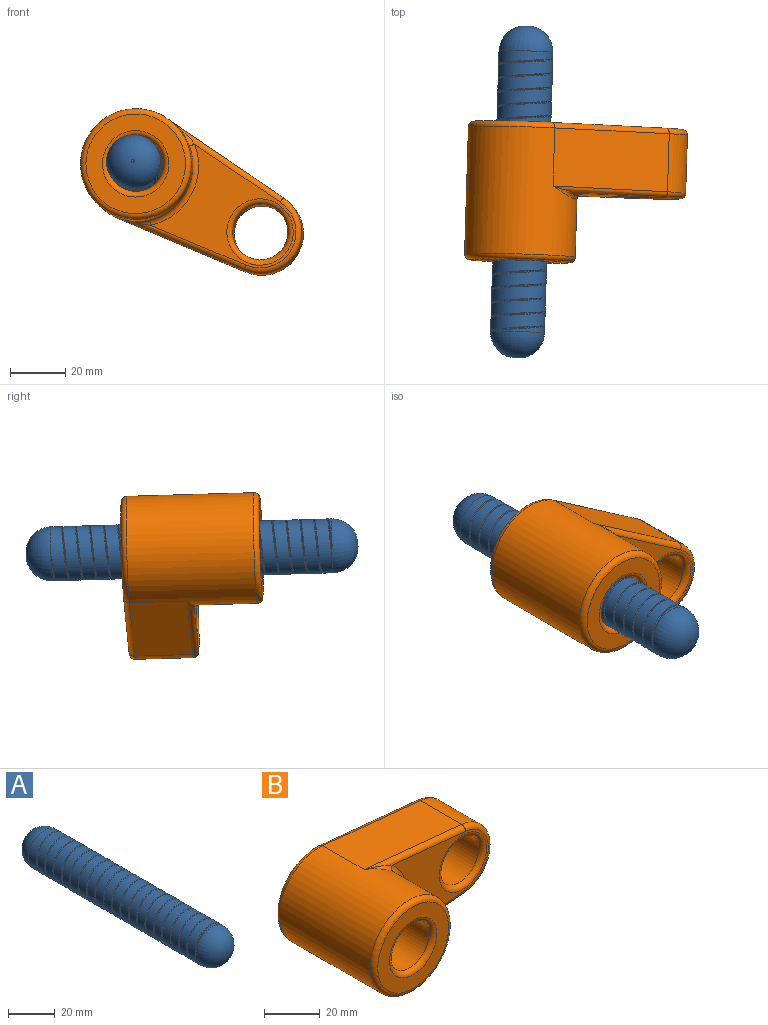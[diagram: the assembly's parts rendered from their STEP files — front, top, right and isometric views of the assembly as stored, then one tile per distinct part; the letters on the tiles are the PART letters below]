
ASSEMBLY  parts=2 mates=1
PART A: 9 faces, bbox 19.9x120x23 mm
  f0: cylinder r=9.75mm len=101.5mm, axis (0,1,0), area 5188.4mm2, adj f1,f4,f5,f6,f7,f8
  f1: torus R=0.5mm, axis (0,-1,0), area 582.8mm2, adj f0,f2,f7,f8
  f2: plane 1x1mm, normal (0,-1,0), area 0.8mm2, adj f1
  f3: plane 1x1mm, normal (0,1,0), area 0.8mm2, adj f4
  f4: torus R=0.5mm, axis (0,-1,0), area 582.8mm2, adj f0,f3,f5,f6
  f5: plane 0.54x0.41mm, normal (0,0,-1), area 0.1mm2, adj f0,f4,f6,f8
  f6: bspline ~101.9x23.01mm, area 579.7mm2, adj f0,f4,f5,f7,f8
  f7: plane 0.54x0.41mm, normal (0,0,1), area 0.1mm2, adj f0,f1,f6,f8
  f8: bspline ~101.93x23.01mm, area 592.1mm2, adj f0,f1,f5,f6,f7
PART B: 24 faces, bbox 88.1x50x43.3 mm
  f0: plane 48.87x33.3mm, normal (0,-1,0), area 703mm2, adj f14,f15,f17,f18,f23
  f1: plane 49.75x21mm, normal (0.1,0,1), area 1050mm2, adj f2,f5,f12,f15
  f2: cylinder r=20mm len=46mm, axis (0,1,0), area 4347.3mm2, adj f1,f3,f10,f13,f14,f16,f20
  f3: plane 49.75x21mm, normal (0.1,0,-1), area 1050mm2, adj f2,f5,f9,f18
  f4: cylinder r=10mm len=21mm, axis (0,1,0), area 1319.5mm2, adj f21,f23
  f5: cylinder r=15mm len=29.85mm, axis (0,1,0), area 926.8mm2, adj f1,f3,f11,f17
  f6: cylinder r=10mm len=46mm, axis (0,1,0), area 2890.3mm2, adj f19,f22
  f7: plane 81.25x36mm, normal (0,1,0), area 1435.1mm2, adj f9,f10,f11,f12,f21,f22
  f8: plane 36x36mm, normal (0,-1,0), area 565.5mm2, adj f19,f20
  f9: cylinder r=2mm len=49.95mm, axis (1,0,0.1), area 157.1mm2, adj f3,f7,f10,f11
  f10: torus R=18mm, axis (0,-1,0), area 202.3mm2, adj f2,f7,f9,f12
  f11: torus R=13mm, axis (0,-1,0), area 131.9mm2, adj f5,f7,f9,f12
  f12: cylinder r=2mm len=49.95mm, axis (-1,0,0.1), area 157.1mm2, adj f1,f7,f10,f11
  f13: bspline ~12.65x4.96mm, area 19.4mm2, adj f2,f14,f15
  f14: torus R=22mm, axis (0,-1,0), area 111.8mm2, adj f0,f2,f13,f16
  f15: cylinder r=2mm len=49.95mm, axis (1,0,-0.1), area 135.6mm2, adj f0,f1,f13,f17
  f16: bspline ~12.65x4.96mm, area 19.4mm2, adj f2,f14,f18
  f17: torus R=13mm, axis (0,-1,0), area 131.9mm2, adj f0,f5,f15,f18
  f18: cylinder r=2mm len=49.95mm, axis (-1,0,-0.1), area 135.6mm2, adj f0,f3,f16,f17
  f19: torus R=12mm, axis (0,-1,0), area 211.7mm2, adj f6,f8
  f20: torus R=18mm, axis (0,-1,0), area 380.4mm2, adj f2,f8
  f21: torus R=12mm, axis (0,-1,0), area 211.7mm2, adj f4,f7
  f22: torus R=12mm, axis (0,-1,0), area 211.7mm2, adj f6,f7
  f23: torus R=12mm, axis (0,-1,0), area 211.7mm2, adj f0,f4
PLACE A rot(axis=(-0.32,-0.89,-0.31),5.3deg) t=(-8.84,-9.4,-9.03)mm
PLACE B rot(axis=(-0.04,1,-0.07),28.5deg) t=(-9.29,-24.39,-8.6)mm
MATE cylindrical A.f0 <-> B.f6  axis (0.03,1,-0.03) through (-10.04,-49.37,-7.89)mm
